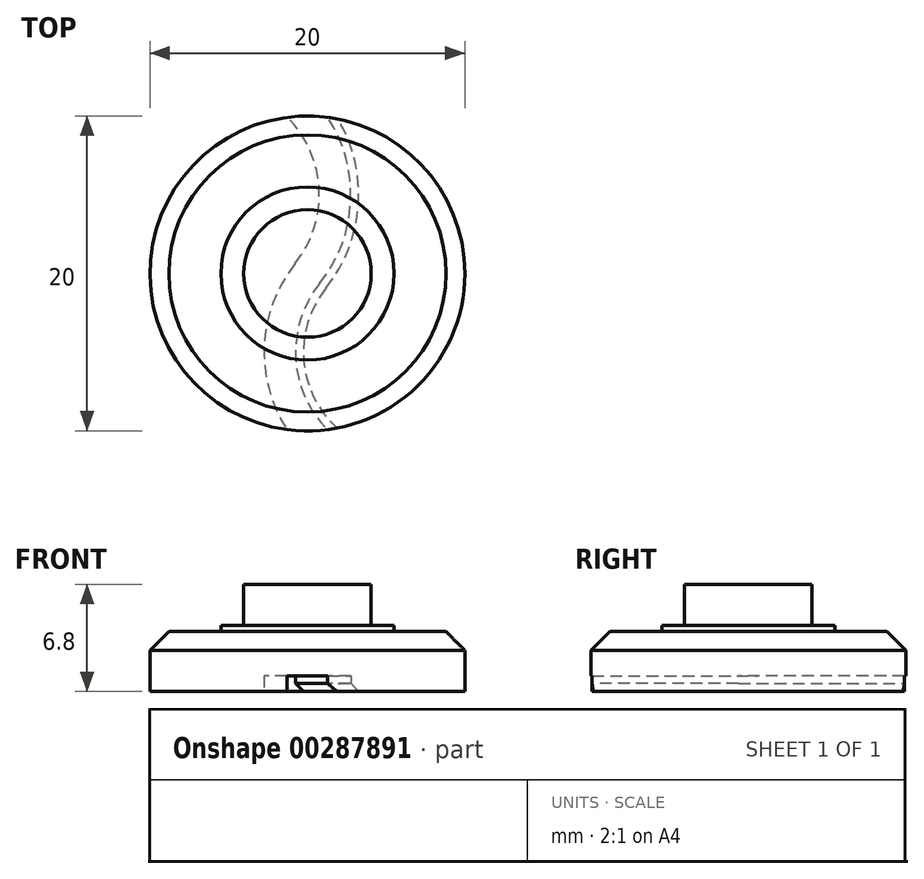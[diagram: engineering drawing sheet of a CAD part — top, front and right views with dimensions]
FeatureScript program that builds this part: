
annotation { "Feature Type Name" : "Feature", "Feature Type Description" : "" }
export const myFeature = defineFeature(function(context is Context, id is Id, definition is map)
    precondition{}
    {
        {
            var Q0;
            Q0=qCreatedBy(makeId("Top.planeOp"),FACE);
            var sketch = newSketch(context, id + "F0", { "sketchPlane" : qUnion([Q0])});
            skCircle(sketch, "E0", {"center": v(0, 0) * mm, "radius": 10 * mm});
            skCircle(sketch, "E1", {"center": v(0, 0) * mm, "radius": 4.05 * mm});
            skCircle(sketch, "E2", {"center": v(0, 0) * mm, "radius": 5.5 * mm});
            skSolve(sketch);
        }
        {
            var Q0;
            Q0=makeQuery(id+"F0.imprint","IMPRINT",FACE,{"disambiguationData":[TD([[makeQuery(id+"F0.imprint","IMPRINT",EDGE,{"derivedFrom":sQuery(id+"F0.wireOp",EDGE,"E0")}),1.0]])]});
            var Q1;
            Q1=makeQuery(id+"F0.imprint","IMPRINT",FACE,{"disambiguationData":[TD([[makeQuery(id+"F0.imprint","IMPRINT",EDGE,{"derivedFrom":sQuery(id+"F0.wireOp",EDGE,"E1")}),1.0]])]});
            var Q2;
            Q2=makeQuery(id+"F0.imprint","IMPRINT",FACE,{"disambiguationData":[TD([[makeQuery(id+"F0.imprint","IMPRINT",EDGE,{"derivedFrom":sQuery(id+"F0.wireOp",EDGE,"E1")}),-1.0]])]});
            extrude(context, id + "F1", {"entities" : qUnion([Q0, Q1, Q2]), "depth" : 3.8 * mm});
        }
        {
            var Q0;
            Q0=makeQuery(id+"F0.imprint","IMPRINT",FACE,{"disambiguationData":[TD([[makeQuery(id+"F0.imprint","IMPRINT",EDGE,{"derivedFrom":sQuery(id+"F0.wireOp",EDGE,"E1")}),1.0]])]});
            extrude(context, id + "F2", {"entities" : qUnion([Q0]), "operationType" : NewBodyOperationType.ADD, "depth" : 6.8 * mm});
        }
        {
            var Q0;
            Q0=makeQuery(id+"F1.opExtrude","CAP_EDGE",EDGE,{"disambiguationData":[OSD([sQuery(id+"F0.wireOp",EDGE,"E0")])],"isStart":false});
            chamfer(context, id + "F3", {"entities" : qUnion([Q0]), "width" : 1.2 * mm, "tangentPropagation" : true});
        }
        {
            var Q0;
            Q0=makeQuery(id+"F0.imprint","IMPRINT",FACE,{"disambiguationData":[TD([[makeQuery(id+"F0.imprint","IMPRINT",EDGE,{"derivedFrom":sQuery(id+"F0.wireOp",EDGE,"E1")}),-1.0]])]});
            extrude(context, id + "F4", {"entities" : qUnion([Q0]), "operationType" : NewBodyOperationType.ADD, "depth" : 4.2 * mm});
        }
        {
            var Q0;
            Q0=makeQuery(id+"F1.opExtrude","CAP_FACE",FACE,{"disambiguationData":[OSD([sQuery(id+"F0.wireOp",EDGE,"E0")])],"isStart":true});
            var sketch = newSketch(context, id + "F5", { "sketchPlane" : qUnion([Q0])});
            skArc(sketch, "E3", {"start": v(0, 10) * mm, "mid": v(-1.76, 5) * mm, "end": v(0, 0) * mm});
            skLineSegment(sketch, "E4", {"start": v(0, 0) * mm, "end": v(10, 0) * mm});
            skArc(sketch, "E5", {"start": v(0, -10) * mm, "mid": v(1.76, -5) * mm, "end": v(0, 0) * mm});
            skArc(sketch, "E6.0", {"start": v(-1.96, -10.53) * mm, "mid": v(0.7, -5.83) * mm, "end": v(-0.78, -0.63) * mm});
            skArc(sketch, "E6.1", {"start": v(-0.78, 10.62) * mm, "mid": v(-2.76, 5) * mm, "end": v(-0.78, -0.63) * mm});
            skArc(sketch, "E7.0", {"start": v(0.78, -10.62) * mm, "mid": v(2.76, -5) * mm, "end": v(0.78, 0.62) * mm});
            skArc(sketch, "E7.1", {"start": v(1.57, 10.2) * mm, "mid": v(-0.73, 5.57) * mm, "end": v(0.78, 0.62) * mm});
            skSolve(sketch);
        }
        {
            var Q0;
            {var subQ7=sQuery(id+"F5.wireOp",EDGE,"E3");Q0=makeQuery(id+"F5.imprint","IMPRINT",FACE,{"disambiguationData":[TD([[makeQuery(id+"F5.imprint","IMPRINT",EDGE,{"derivedFrom":subQ7}),-1.0]])]});}
            var Q1;
            {var subQ7=sQuery(id+"F5.wireOp",EDGE,"E3");Q1=makeQuery(id+"F5.imprint","IMPRINT",FACE,{"disambiguationData":[TD([[makeQuery(id+"F5.imprint","IMPRINT",EDGE,{"derivedFrom":subQ7}),1.0]])]});}
            var Q2;
            {var subQ0=sQuery(id+"F5.wireOp",EDGE,"E5");Q2=makeQuery(id+"F5.imprint","IMPRINT",FACE,{"disambiguationData":[TD([[makeQuery(id+"F5.imprint","IMPRINT",EDGE,{"derivedFrom":subQ0}),-1.0]])]});}
            extrude(context, id + "F6", {"entities" : qUnion([Q0, Q1, Q2]), "operationType" : NewBodyOperationType.REMOVE, "oppositeDirection" : true, "depth" : 1 * mm, "offsetDistance" : 25 * mm});
        }
        {
            var Q0;
            Q0=makeQuery(id+"F6.boolean.opBoolean","COPY",EDGE,{"derivedFrom":makeQuery(id+"F6.opExtrude","CAP_EDGE",EDGE,{"disambiguationData":[OSD([sQuery(id+"F5.wireOp",EDGE,"E6.1")])],"isStart":true})});
            var Q1;
            Q1=makeQuery(id+"F6.boolean.opBoolean","COPY",EDGE,{"derivedFrom":makeQuery(id+"F6.opExtrude","CAP_EDGE",EDGE,{"disambiguationData":[OSD([sQuery(id+"F5.wireOp",EDGE,"E6.0")])],"isStart":true})});
            var Q2;
            Q2=makeQuery(id+"F6.boolean.opBoolean","COPY",EDGE,{"derivedFrom":makeQuery(id+"F6.opExtrude","CAP_EDGE",EDGE,{"disambiguationData":[OSD([sQuery(id+"F5.wireOp",EDGE,"E7.0")])],"isStart":true})});
            var Q3;
            Q3=makeQuery(id+"F6.boolean.opBoolean","COPY",EDGE,{"derivedFrom":makeQuery(id+"F6.opExtrude","CAP_EDGE",EDGE,{"disambiguationData":[OSD([sQuery(id+"F5.wireOp",EDGE,"E7.1")])],"isStart":true})});
            chamfer(context, id + "F7", {"entities" : qUnion([Q0, Q1, Q2, Q3]), "chamferType" : ChamferType.TWO_OFFSETS, "width1" : .5 * mm, "oppositeDirection" : false, "width2" : .5 * mm, "tangentPropagation" : true});
        }
    });
